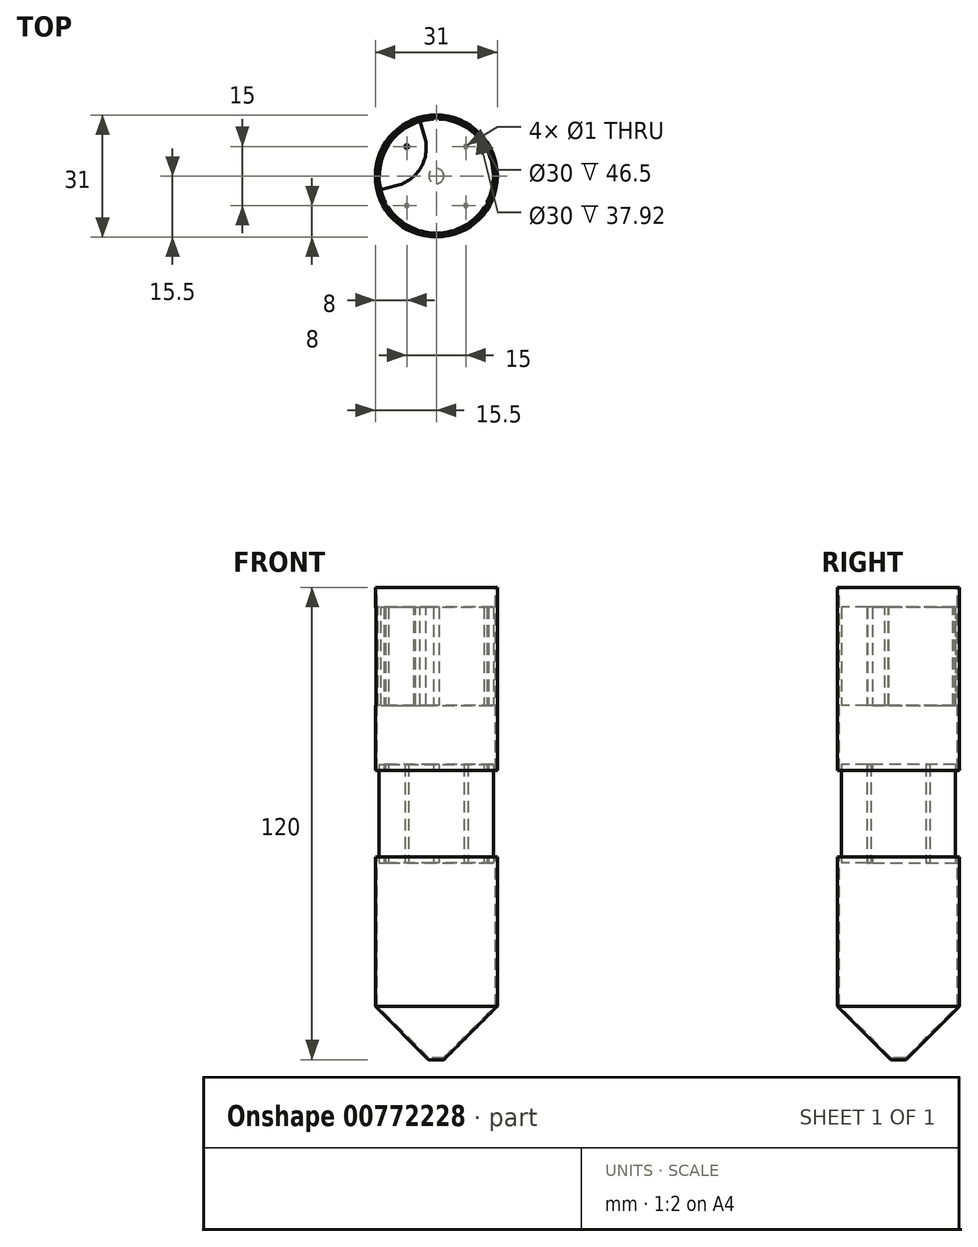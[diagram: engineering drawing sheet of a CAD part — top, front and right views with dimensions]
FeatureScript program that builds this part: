
annotation { "Feature Type Name" : "Feature", "Feature Type Description" : "" }
export const myFeature = defineFeature(function(context is Context, id is Id, definition is map)
    precondition{}
    {
        {
            var Q0;
            Q0=qCreatedBy(makeId("Front.planeOp"),FACE);
            var sketch = newSketch(context, id + "F0", { "sketchPlane" : qUnion([Q0])});
            skLineSegment(sketch, "E0", {"start": v(0, 0) * mm, "end": v(1.92, 0) * mm});
            skLineSegment(sketch, "E1", {"start": v(1.92, 0) * mm, "end": v(15.5, 13.58) * mm});
            skLineSegment(sketch, "E2", {"start": v(15.5, 13.58) * mm, "end": v(15.5, 120) * mm});
            skLineSegment(sketch, "E3", {"start": v(15.5, 120) * mm, "end": v(15, 120) * mm});
            skLineSegment(sketch, "E4", {"start": v(15, 120) * mm, "end": v(15, 13.58) * mm});
            skLineSegment(sketch, "E5", {"start": v(15, 13.58) * mm, "end": v(1.92, 0.5) * mm});
            skLineSegment(sketch, "E6", {"start": v(1.92, 0.5) * mm, "end": v(0, 0.5) * mm});
            skLineSegment(sketch, "E7", {"start": v(0, 0.5) * mm, "end": v(0, 0) * mm});
            skSolve(sketch);
        }
        {
            var Q0;
            Q0 = qSketchRegion(id + "F0", true);
            var Q1;
            Q1=sQuery(id+"F0.wireOp",EDGE,"E7");
            revolve(context, id + "F1", {"surfaceOperationType" : NewSurfaceOperationType.NEW, "entities" : qUnion([Q0]), "axis" : qUnion([Q1]), "revolveType" : RevolveType.FULL});
        }
        {
            var Q0;
            Q0=qCreatedBy(makeId("Top.planeOp"),FACE);
            cPlane(context, id + "F2", {"entities" : qUnion([Q0]), "cplaneType" : CPlaneType.OFFSET, "offset" : 50 * mm, "width" : 150 * mm, "height" : 150 * mm});
        }
        {
            var Q0;
            Q0=qCreatedBy(id+"F2.planeOp",FACE);
            var sketch = newSketch(context, id + "F3", { "sketchPlane" : qUnion([Q0])});
            skCircle(sketch, "E8.0", {"center": v(0, 0) * mm, "radius": 15 * mm, "construction": true});
            skCircle(sketch, "E9", {"center": v(0, 0) * mm, "radius": 14.5 * mm});
            skLineSegment(sketch, "E10", {"start": v(0, 0) * mm, "end": v(0, 14.5) * mm, "construction": true});
            skLineSegment(sketch, "E11", {"start": v(0, 0) * mm, "end": v(-12.56, -7.25) * mm, "construction": true});
            skLineSegment(sketch, "E12", {"start": v(0, 0) * mm, "end": v(12.56, -7.25) * mm, "construction": true});
            skCircle(sketch, "E13", {"center": v(0, 14.5) * mm, "radius": 0.75 * mm});
            skCircle(sketch, "E14", {"center": v(12.56, -7.25) * mm, "radius": 0.75 * mm});
            skCircle(sketch, "E15", {"center": v(-12.56, -7.25) * mm, "radius": 0.75 * mm});
            skPoint(sketch, "E16", {"position": v(0, 15) * mm});
            skPoint(sketch, "E17", {"position": v(0, 15.25) * mm});
            skLineSegment(sketch, "E18.bottom", {"start": v(-7.5, 7.5) * mm, "end": v(7.5, 7.5) * mm, "construction": true});
            skLineSegment(sketch, "E18.top", {"start": v(-7.5, -7.5) * mm, "end": v(7.5, -7.5) * mm, "construction": true});
            skLineSegment(sketch, "E18.left", {"start": v(-7.5, 7.5) * mm, "end": v(-7.5, -7.5) * mm, "construction": true});
            skLineSegment(sketch, "E18.right", {"start": v(7.5, 7.5) * mm, "end": v(7.5, -7.5) * mm, "construction": true});
            skCircle(sketch, "E19", {"center": v(-7.5, 7.5) * mm, "radius": 0.5 * mm});
            skCircle(sketch, "E20", {"center": v(7.5, 7.5) * mm, "radius": 0.5 * mm});
            skCircle(sketch, "E21", {"center": v(7.5, -7.5) * mm, "radius": 0.5 * mm});
            skCircle(sketch, "E22", {"center": v(-7.5, -7.5) * mm, "radius": 0.5 * mm});
            skSolve(sketch);
        }
        {
            var Q0;
            Q0 = qSketchRegion(id + "F3", true);
            extrude(context, id + "F4", {"entities" : qUnion([Q0]), "depth" : 25 * mm, "offsetDistance" : 25 * mm});
        }
        {
            var Q0;
            Q0=makeQuery(id+"F4.opExtrude","CAP_FACE",FACE,{"disambiguationData":[OSD([sQuery(id+"F3.wireOp",EDGE,"E9"),sQuery(id+"F3.wireOp",EDGE,"E13"),sQuery(id+"F3.wireOp",EDGE,"E14"),sQuery(id+"F3.wireOp",EDGE,"E15"),sQuery(id+"F3.wireOp",EDGE,"E19"),sQuery(id+"F3.wireOp",EDGE,"E20"),sQuery(id+"F3.wireOp",EDGE,"E21"),sQuery(id+"F3.wireOp",EDGE,"E22")])],"isStart":false});
            cPlane(context, id + "F5", {"entities" : qUnion([Q0]), "cplaneType" : CPlaneType.OFFSET, "offset" : 15 * mm, "width" : 150 * mm, "height" : 150 * mm});
        }
        {
            var Q0;
            Q0=qCreatedBy(id+"F5.planeOp",FACE);
            var sketch = newSketch(context, id + "F6", { "sketchPlane" : qUnion([Q0])});
            skArc(sketch, "E23.0.0", {"start": v(0.75, 14.48) * mm, "mid": v(0, 15.25) * mm, "end": v(-0.75, 14.48) * mm});
            skArc(sketch, "E23.0.1", {"start": v(-0.75, 14.48) * mm, "mid": v(-12.56, 7.25) * mm, "end": v(-12.92, -6.6) * mm});
            skArc(sketch, "E23.0.2", {"start": v(-12.92, -6.6) * mm, "mid": v(-13.2, -7.62) * mm, "end": v(-12.17, -7.89) * mm});
            skArc(sketch, "E23.0.3", {"start": v(-12.17, -7.89) * mm, "mid": v(0, -14.5) * mm, "end": v(12.17, -7.89) * mm});
            skArc(sketch, "E23.0.4", {"start": v(12.17, -7.89) * mm, "mid": v(13.2, -7.62) * mm, "end": v(12.92, -6.6) * mm});
            skArc(sketch, "E23.0.5", {"start": v(12.92, -6.6) * mm, "mid": v(12.56, 7.25) * mm, "end": v(0.75, 14.48) * mm});
            skCircle(sketch, "E24.0", {"center": v(7.5, 7.5) * mm, "radius": 0.5 * mm, "construction": true});
            skCircle(sketch, "E24.1", {"center": v(-7.5, 7.5) * mm, "radius": 0.5 * mm, "construction": true});
            skCircle(sketch, "E24.2", {"center": v(-7.5, -7.5) * mm, "radius": 0.5 * mm, "construction": true});
            skCircle(sketch, "E24.3", {"center": v(7.5, -7.5) * mm, "radius": 0.5 * mm, "construction": true});
            skCircle(sketch, "E25", {"center": v(-7.5, 7.5) * mm, "radius": 1.52 * mm});
            skSolve(sketch);
        }
        {
            var Q0;
            Q0=makeQuery(id+"F6.imprint","IMPRINT",FACE,{"disambiguationData":[TD([[makeQuery(id+"F6.imprint","IMPRINT",EDGE,{"derivedFrom":sQuery(id+"F6.wireOp",EDGE,"E23.0.0")}),1.0]])]});
            extrude(context, id + "F7", {"entities" : qUnion([Q0]), "depth" : 25 * mm, "offsetDistance" : 25 * mm});
        }
        {
            var Q0;
            Q0=makeQuery(id+"F7.opExtrude","CAP_FACE",FACE,{"disambiguationData":[OSD([sQuery(id+"F6.wireOp",EDGE,"E23.0.0"),sQuery(id+"F6.wireOp",EDGE,"E23.0.1"),sQuery(id+"F6.wireOp",EDGE,"E23.0.2"),sQuery(id+"F6.wireOp",EDGE,"E23.0.3"),sQuery(id+"F6.wireOp",EDGE,"E23.0.4"),sQuery(id+"F6.wireOp",EDGE,"E23.0.5"),sQuery(id+"F6.wireOp",EDGE,"E25")])],"isStart":false});
            var sketch = newSketch(context, id + "F8", { "sketchPlane" : qUnion([Q0])});
            skLineSegment(sketch, "E26", {"start": v(0, 0) * mm, "end": v(-12.56, 7.25) * mm, "construction": true});
            skLineSegment(sketch, "E27", {"start": v(0, 0) * mm, "end": v(0, 14.5) * mm, "construction": true});
            skLineSegment(sketch, "E28", {"start": v(0, 0) * mm, "end": v(12.56, 7.25) * mm, "construction": true});
            skLineSegment(sketch, "E29", {"start": v(0, 0) * mm, "end": v(0, -14.5) * mm, "construction": true});
            skCircle(sketch, "E30", {"center": v(-12.56, 7.25) * mm, "radius": 10 * mm});
            skLineSegment(sketch, "E31", {"start": v(0, 0) * mm, "end": v(-14.1, -3.41) * mm});
            skLineSegment(sketch, "E32", {"start": v(0, 0) * mm, "end": v(-4.1, 13.91) * mm});
            skSolve(sketch);
        }
        {
            var Q0;
            Q0=makeQuery(id+"F8.imprint","IMPRINT",FACE,{"disambiguationData":[TD([[makeQuery(id+"F8.imprint","IMPRINT",EDGE,{"derivedFrom":makeQuery(id+"F7.opExtrude","CAP_EDGE",EDGE,{"disambiguationData":[OSD([sQuery(id+"F6.wireOp",EDGE,"E25")])],"isStart":false})}),1.0]])]});
            var Q1;
            {var subQ0=sQuery(id+"F8.wireOp",EDGE,"E30");var subQ1=makeQuery(id+"F7.opExtrude","CAP_EDGE",EDGE,{"disambiguationData":[OSD([sQuery(id+"F6.wireOp",EDGE,"E23.0.1")])],"isStart":false});var subQ2=makeQuery(id+"F8.imprint","INTERSECT",VERTEX,{"disambiguationData":[OD(0.0)],"derivedFrom":[subQ1,subQ0]});Q1=makeQuery(id+"F8.imprint","IMPRINT",FACE,{"disambiguationData":[TD([[makeQuery(id+"F8.imprint","IMPRINT",EDGE,{"disambiguationData":[TD([[subQ2,-1.0]])],"derivedFrom":subQ0}),1.0]])]});}
            var Q2;
            Q2=makeQuery(id+"F8.imprint","IMPRINT",FACE,{"disambiguationData":[TD([[makeQuery(id+"F8.imprint","IMPRINT",EDGE,{"derivedFrom":makeQuery(id+"F7.opExtrude","CAP_EDGE",EDGE,{"disambiguationData":[OSD([sQuery(id+"F6.wireOp",EDGE,"E25")])],"isStart":false})}),-1.0]])]});
            var Q3;
            {var subQ0=sQuery(id+"F8.wireOp",EDGE,"E32");var subQ1=sQuery(id+"F8.wireOp",EDGE,"E30");var subQ2=makeQuery(id+"F8.imprint","INTERSECT",VERTEX,{"derivedFrom":[subQ1,subQ0]});Q3=makeQuery(id+"F8.imprint","IMPRINT",FACE,{"disambiguationData":[TD([[makeQuery(id+"F8.imprint","IMPRINT",EDGE,{"disambiguationData":[TD([[subQ2,-1.0]])],"derivedFrom":subQ1}),-1.0]])]});}
            var Q4;
            {var subQ0=sQuery(id+"F8.wireOp",EDGE,"E31");var subQ1=sQuery(id+"F8.wireOp",EDGE,"E30");var subQ2=makeQuery(id+"F8.imprint","INTERSECT",VERTEX,{"derivedFrom":[subQ1,subQ0]});Q4=makeQuery(id+"F8.imprint","IMPRINT",FACE,{"disambiguationData":[TD([[makeQuery(id+"F8.imprint","IMPRINT",EDGE,{"disambiguationData":[TD([[subQ2,1.0]])],"derivedFrom":subQ1}),-1.0]])]});}
            extrude(context, id + "F9", {"entities" : qUnion([Q0, Q1, Q2, Q3, Q4]), "operationType" : NewBodyOperationType.REMOVE, "oppositeDirection" : true, "depth" : 25 * mm, "offsetDistance" : 25 * mm});
        }
        {
            var Q0;
            Q0=makeQuery(id+"F4.opExtrude","CAP_FACE",FACE,{"disambiguationData":[OSD([sQuery(id+"F3.wireOp",EDGE,"E9"),sQuery(id+"F3.wireOp",EDGE,"E13"),sQuery(id+"F3.wireOp",EDGE,"E14"),sQuery(id+"F3.wireOp",EDGE,"E15"),sQuery(id+"F3.wireOp",EDGE,"E19"),sQuery(id+"F3.wireOp",EDGE,"E20"),sQuery(id+"F3.wireOp",EDGE,"E21"),sQuery(id+"F3.wireOp",EDGE,"E22")])],"isStart":false});
            cPlane(context, id + "F10", {"entities" : qUnion([Q0]), "cplaneType" : CPlaneType.OFFSET, "offset" : 1.5 * mm, "oppositeDirection" : true, "width" : 150 * mm, "height" : 150 * mm});
        }
        {
            var Q0;
            Q0=makeQuery(id+"F4.opExtrude","CAP_FACE",FACE,{"disambiguationData":[OSD([sQuery(id+"F3.wireOp",EDGE,"E9"),sQuery(id+"F3.wireOp",EDGE,"E13"),sQuery(id+"F3.wireOp",EDGE,"E14"),sQuery(id+"F3.wireOp",EDGE,"E15"),sQuery(id+"F3.wireOp",EDGE,"E19"),sQuery(id+"F3.wireOp",EDGE,"E20"),sQuery(id+"F3.wireOp",EDGE,"E21"),sQuery(id+"F3.wireOp",EDGE,"E22")])],"isStart":true});
            cPlane(context, id + "F11", {"entities" : qUnion([Q0]), "cplaneType" : CPlaneType.OFFSET, "offset" : 1.5 * mm, "oppositeDirection" : true, "width" : 150 * mm, "height" : 150 * mm});
        }
        {
            var Q0;
            Q0=qCreatedBy(id+"F10.planeOp",FACE);
            var sketch = newSketch(context, id + "F12", { "sketchPlane" : qUnion([Q0])});
            skArc(sketch, "E33.0", {"start": v(-12.17, -7.89) * mm, "mid": v(0, -14.5) * mm, "end": v(12.17, -7.89) * mm});
            skCircle(sketch, "E34", {"center": v(0, 0) * mm, "radius": 14.5 * mm});
            skCircle(sketch, "E35", {"center": v(0, 0) * mm, "radius": 20.8 * mm});
            skSolve(sketch);
        }
        {
            var Q0;
            Q0=makeQuery(id+"F12.imprint","IMPRINT",FACE,{"disambiguationData":[TD([[makeQuery(id+"F12.imprint","IMPRINT",EDGE,{"derivedFrom":sQuery(id+"F12.wireOp",EDGE,"E35")}),1.0]])]});
            var Q1;
            Q1=qCreatedBy(id+"F11.planeOp",FACE);
            extrude(context, id + "F13", {"entities" : qUnion([Q0]), "operationType" : NewBodyOperationType.REMOVE, "endBound" : BoundingType.UP_TO_SURFACE, "oppositeDirection" : true, "depth" : 25 * mm, "endBoundEntityFace" : qUnion([Q1]), "offsetDistance" : 25 * mm});
        }
    });
